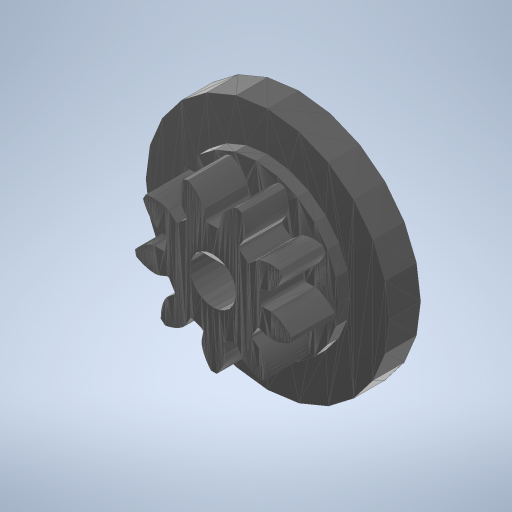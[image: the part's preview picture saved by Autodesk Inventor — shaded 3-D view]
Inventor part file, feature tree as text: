
AUTODESK INVENTOR PART (.ipt)
format: ipt  version: 2023.2 (Build 272271000, 271)  size: 301,056 bytes
history: native  units: mm
features: other x2, extrude x1, sketch x1
ambient origin geometry x8: Origin, YZ Plane, XZ Plane, XY Plane, X Axis, Y Axis, Z Axis, Center Point
bodies: Volumenkörper1 (feature_tree)
feature tree (4):
  other  "6a_gear_100"
  extrude  "Extrusion1"  Depth=9.4mm TaperAngle=0.0deg
  sketch  "Skizze1"  dims[d0=2.1mm d1=9.4mm d2=0.0mm]
  other  "MeshFeature1"
